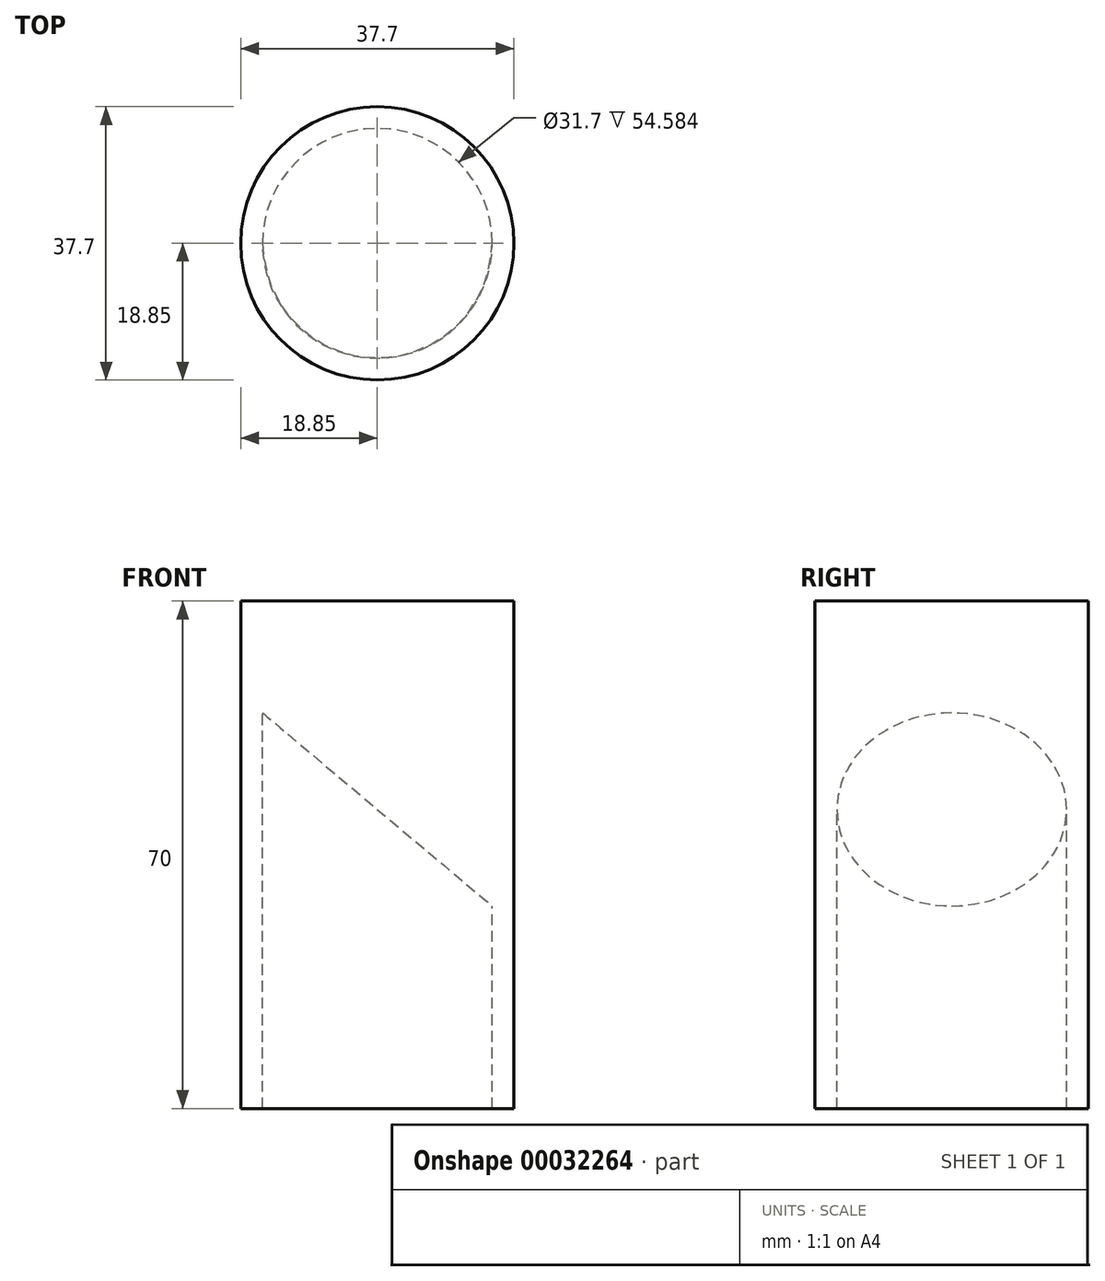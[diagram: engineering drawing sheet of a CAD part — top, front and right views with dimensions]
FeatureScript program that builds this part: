
annotation { "Feature Type Name" : "Feature", "Feature Type Description" : "" }
export const myFeature = defineFeature(function(context is Context, id is Id, definition is map)
    precondition{}
    {
        {
            var Q0;
            Q0=qCreatedBy(makeId("Top.planeOp"),FACE);
            var sketch = newSketch(context, id + "F0", { "sketchPlane" : qUnion([Q0])});
            skCircle(sketch, "E0", {"center": v(0, 0) * mm, "radius": 15.85 * mm});
            skCircle(sketch, "E1.0", {"center": v(0, 0) * mm, "radius": 18.85 * mm});
            skSolve(sketch);
        }
        {
            var Q0;
            Q0 = qSketchRegion(id + "F0", true);
            extrude(context, id + "F1", {"entities" : qUnion([Q0]), "oppositeDirection" : true, "depth" : 70 * mm});
        }
        {
            var Q0;
            Q0=qCreatedBy(makeId("Front.planeOp"),FACE);
            var sketch = newSketch(context, id + "F2", { "sketchPlane" : qUnion([Q0])});
            skLineSegment(sketch, "E2", {"start": v(-18.85, -12.9) * mm, "end": v(18.85, -44.6) * mm});
            skLineSegment(sketch, "E3", {"start": v(0, -28.75) * mm, "end": v(10.37, -16.42) * mm});
            skSolve(sketch);
        }
        {
            var Q0;
            Q0=sQuery(id+"F2.wireOp",VERTEX,"E3.start");
            var Q1;
            Q1=sQuery(id+"F2.wireOp",EDGE,"E3");
            cPlane(context, id + "F3", {"entities" : qUnion([Q0, Q1]), "cplaneType" : CPlaneType.LINE_POINT, "offset" : 150 * mm, "width" : 150 * mm, "height" : 150 * mm});
        }
        {
            var Q0;
            Q0=makeQuery(id+"F1.opExtrude","CAP_FACE",FACE,{"disambiguationData":[OSD([sQuery(id+"F0.wireOp",EDGE,"E0"),sQuery(id+"F0.wireOp",EDGE,"E1.0")])],"isStart":true});
            var sketch = newSketch(context, id + "F4", { "sketchPlane" : qUnion([Q0])});
            skCircle(sketch, "E4.0", {"center": v(0, 0) * mm, "radius": 18.85 * mm});
            skSolve(sketch);
        }
        {
            var Q0;
            Q0 = qSketchRegion(id + "F4", true);
            var Q1;
            Q1=qCreatedBy(id+"F3.planeOp",FACE);
            extrude(context, id + "F5", {"entities" : qUnion([Q0]), "operationType" : NewBodyOperationType.ADD, "endBound" : BoundingType.UP_TO_SURFACE, "oppositeDirection" : true, "endBoundEntityFace" : qUnion([Q1]), "depth" : 25 * mm});
        }
    });
